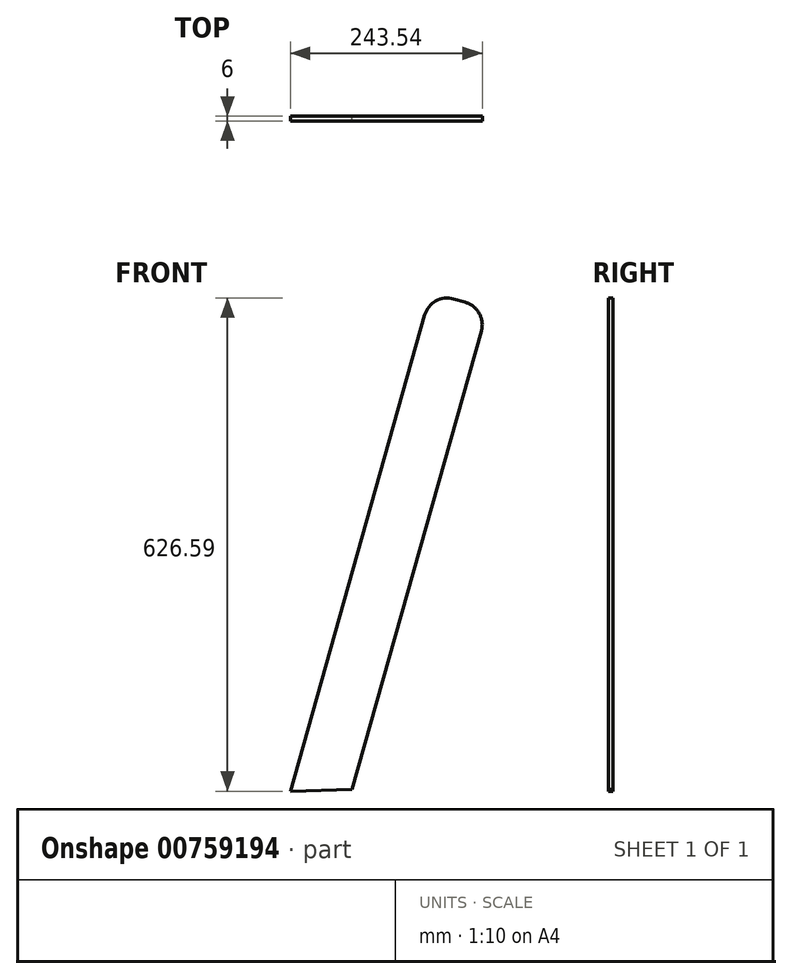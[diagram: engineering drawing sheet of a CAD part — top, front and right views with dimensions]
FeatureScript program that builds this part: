
annotation { "Feature Type Name" : "Feature", "Feature Type Description" : "" }
export const myFeature = defineFeature(function(context is Context, id is Id, definition is map)
    precondition{}
    {
        {
            var Q0;
            Q0=qCreatedBy(makeId("Front.planeOp"),FACE);
            var sketch = newSketch(context, id + "F0", { "sketchPlane" : qUnion([Q0])});
            skLineSegment(sketch, "E0", {"start": v(34.8, -20.11) * mm, "end": v(205.64, 586.79) * mm});
            skLineSegment(sketch, "E1", {"start": v(242.6, 607.55) * mm, "end": v(257.05, 603.5) * mm});
            skPoint(sketch, "E2.visualSharp", {"position": v(285.98, 595.4) * mm});
            skArc(sketch, "E2.filletArc", {"start": v(277.84, 566.48) * mm, "mid": v(275.12, 589.3) * mm, "end": v(257.05, 603.5) * mm});
            skPoint(sketch, "E3.visualSharp", {"position": v(213.76, 615.63) * mm});
            skArc(sketch, "E3.filletArc", {"start": v(242.6, 607.55) * mm, "mid": v(219.83, 604.82) * mm, "end": v(205.64, 586.79) * mm});
            skLineSegment(sketch, "E4", {"start": v(34.98, -17.95) * mm, "end": v(113.54, -15.67) * mm});
            skLineSegment(sketch, "E5", {"start": v(277.84, 566.48) * mm, "end": v(113.54, -15.67) * mm});
            skSolve(sketch);
        }
        {
            var Q0;
            Q0 = qSketchRegion(id + "F0", true);
            extrude(context, id + "F1", {"entities" : qUnion([Q0]), "depth" : 6 * mm, "offsetDistance" : 25 * mm});
        }
    });
